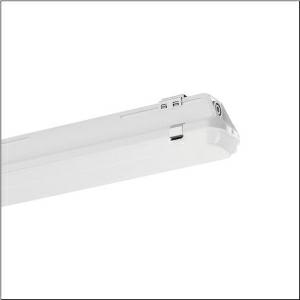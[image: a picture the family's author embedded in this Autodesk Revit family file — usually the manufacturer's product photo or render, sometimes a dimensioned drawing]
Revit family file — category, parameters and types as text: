
# Revit family: monsun_r__21_51fb207l440k_68e8
name_source: partatom
category: Lighting Fixtures
units: mm (PartAtom-declared; Revit-internal decimal feet)

## family parameters
Cut with Voids When Loaded = No
Host = Face
Light Source = No
Part Type = Normal
Room Calculation Point = No
Round Connector Dimension = Use Diameter
Shared = No

## types (1)
- Monsun® 21 (1 x LED, 4330 lm, 27.2 W, 4000K)
    Apparent Load = 27 VA
    CIE Flux Codes = 45 75 93 94 100
    Color Rendering = 80
    Color Temperature = 4000K
    Default Elevation = 1800 mm
    Description = Monsun® 21, damp-proof luminaire, chain hanger, primary optical cover: enclosure, of PC, light emission: direct distribution, primary light characteristic: symmetric, installation type: suspended mounting, surface-mounted, horizontal mounting, vertical mounting, LED, rated luminous flux: 4.330lm, luminous efficacy: 159lm/W, light colour: 840, colour temperature: 4000K, control gear: ON/OFF, with terminal, 3-pole, max. 2.5mm², mains connection: 220..240V, AC, 50/60Hz, rated input power: 27W, housing, of glass-fibre reinforced plastic, uncoated, bright grey, incl. chain hanger, length: 1.299mm, width: 90mm, height: 88mm, clip for enclosure, of stainless steel (V2A), ceiling mounting element, of stainless steel (V2A), chain hanger, of stainless steel (V2A), protection rating (complete): IP66, insulation class (complete): insulation class I (protective earthing), certification: CE, ENEC, VDE, UKCA, protection symbol: D, impact resistance: IK08, permissible operating ambient temperature: -25..+35°C, standard: EN 50419, EN 60598-2-1, corresponds to IFS (International Featured Standards) requirements for safety and quality in the food industry, for indoor or canopied outdoor use, no direct snow, no direct sun, no direct rain, LABS conformity tested according to VDMA 24364:2018-05, contact your sales advisor before using the luminaires in applications with unclear chemical exposure, large temperature fluctuations or condensation-forming humidity, packaging unit: 1 piece
    Height = 88 mm
    Lamp = 1 x LED
    Lamp Light Flux = 4330 lm
    Lamp Power = 27.2 W
    Lamp count = 1
    Length = 1299 mm
    Luminous efficacy = 159 lm/W
    Manufacturer = Siteco
    ModVariant = No
    Model = 51FB207L440K
    Mounting Place = Ceiling
    Mounting Type = Surface mounted
    Number of Poles = 1
    OnlyDefault = Yes
    Power Factor = 1
    Product Name = Monsun® 21
    Product group = damp-proof luminaire
    ProductGroupID = 301
    Protection Class = Protection class I
    Protection Degree = IP 66
    RLX_Detail_Level = 1
    RLX_Emergency_Light_Flux = 0 lm
    RLX_Emergency_Type = 0
    RLX_Emergency_Type_DB = No
    RlxData = <blob elided: 89673 chars, md5=bf5581b2>
    Socket = socket
    Standby Power = 0 W
    System Light Flux = 4330 lm
    System Power = 27 W
    Type Comments = Product without accessories
    Type Image = l_1319656.jpg
    URL = http://relux.com
    VarID = ---
    Voltage = 0 V
    Weight = 0.00 kg
    Width = 90 mm

## geometry (parser evidence)
native form markers: Blend x4, Sweep x13
no freeform markers — native parametric forms only
